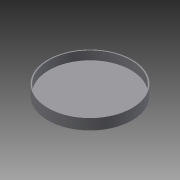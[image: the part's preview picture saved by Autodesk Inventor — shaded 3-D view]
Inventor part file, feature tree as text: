
AUTODESK INVENTOR PART (.ipt)
format: ipt  version: 2015 (Build 190159000, 159)  size: 78,336 bytes
history: native  units: mm
features: extrude x2, sketch x2
ambient origin geometry x8: Origin, YZ Plane, XZ Plane, XY Plane, X Axis, Y Axis, Z Axis, Center Point
bodies: Solid1 (feature_tree)
feature tree (4):
  extrude  "Extrusion1"  Depth=10.0mm TaperAngle=0.0deg
  extrude  "Extrusion2"  Depth=8.0mm TaperAngle=0.0deg
  sketch  "Sketch1"  dims[d0=78.5mm d1=10.0mm d2=0.0mm]
  sketch  "Sketch2"  dims[d3=76.5mm d4=8.0mm d5=0.0mm]
